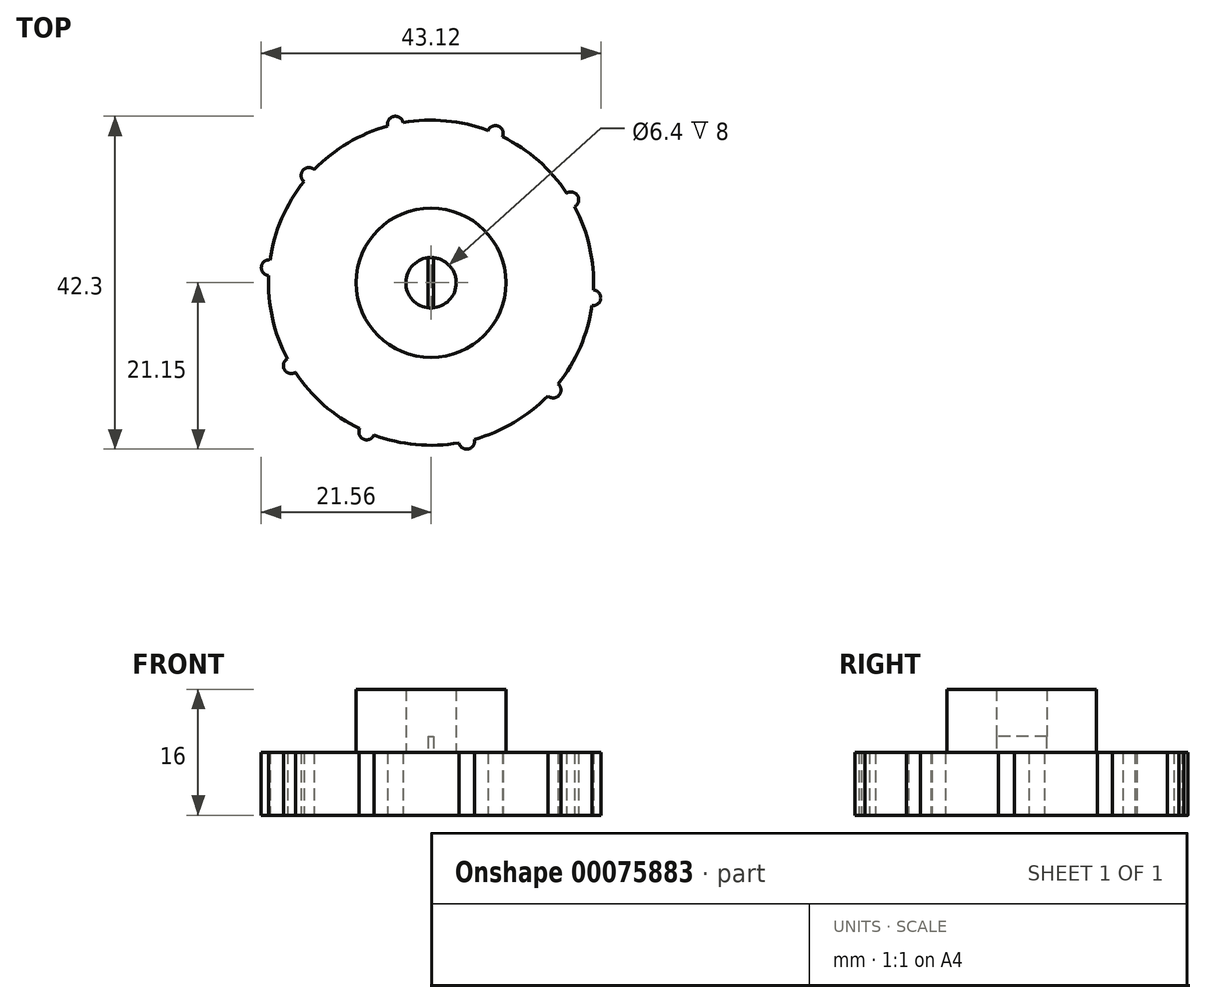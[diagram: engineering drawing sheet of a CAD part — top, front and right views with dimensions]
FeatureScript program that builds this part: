
annotation { "Feature Type Name" : "Feature", "Feature Type Description" : "" }
export const myFeature = defineFeature(function(context is Context, id is Id, definition is map)
    precondition{}
    {
        {
            var Q0;
            Q0=qCreatedBy(makeId("Top.planeOp"),FACE);
            var sketch = newSketch(context, id + "F0", { "sketchPlane" : qUnion([Q0])});
            skCircle(sketch, "E0", {"center": v(0, 0) * mm, "radius": 20.65 * mm});
            skCircle(sketch, "E1", {"center": v(-15.5, 13.63) * mm, "radius": 1 * mm});
            skCircle(sketch, "E2.1.0", {"center": v(-4.53, 20.15) * mm, "radius": 1 * mm});
            skCircle(sketch, "E2.2.0", {"center": v(8.17, 18.96) * mm, "radius": 1 * mm});
            skCircle(sketch, "E2.3.0", {"center": v(17.76, 10.54) * mm, "radius": 1 * mm});
            skCircle(sketch, "E2.4.0", {"center": v(20.56, -1.91) * mm, "radius": 1 * mm});
            skCircle(sketch, "E2.5.0", {"center": v(15.5, -13.63) * mm, "radius": 1 * mm});
            skCircle(sketch, "E2.6.0", {"center": v(4.53, -20.15) * mm, "radius": 1 * mm});
            skCircle(sketch, "E2.7.0", {"center": v(-8.17, -18.96) * mm, "radius": 1 * mm});
            skCircle(sketch, "E2.8.0", {"center": v(-17.76, -10.54) * mm, "radius": 1 * mm});
            skCircle(sketch, "E2.9.0", {"center": v(-20.56, 1.91) * mm, "radius": 1 * mm});
            skLineSegment(sketch, "E2.anchor1", {"start": v(0, 0) * mm, "end": v(-15.5, 13.63) * mm, "construction": true});
            skLineSegment(sketch, "E2.anchor2", {"start": v(0, 0) * mm, "end": v(-20.56, 1.91) * mm, "construction": true});
            skSolve(sketch);
        }
        {
            var Q0;
            Q0 = qSketchRegion(id + "F0", true);
            extrude(context, id + "F1", {"entities" : qUnion([Q0]), "depth" : 8 * mm});
        }
        {
            var Q0;
            Q0=makeQuery(id+"F1.opExtrude","CAP_FACE",FACE,{"disambiguationData":[OSD([sQuery(id+"F0.wireOp",EDGE,"E0")])],"isStart":false});
            var sketch = newSketch(context, id + "F2", { "sketchPlane" : qUnion([Q0])});
            skCircle(sketch, "E3", {"center": v(0, 0) * mm, "radius": 9.5 * mm});
            skCircle(sketch, "E4", {"center": v(0, 0) * mm, "radius": 3.2 * mm});
            skLineSegment(sketch, "E5.right", {"start": v(3.2, 0) * mm, "end": v(3.2, 0) * mm});
            skSolve(sketch);
        }
        {
            var Q0;
            Q0=makeQuery(id+"F2.imprint","IMPRINT",FACE,{"disambiguationData":[TD([[makeQuery(id+"F2.imprint","IMPRINT",EDGE,{"derivedFrom":sQuery(id+"F2.wireOp",EDGE,"E3")}),1.0]])]});
            extrude(context, id + "F3", {"entities" : qUnion([Q0]), "operationType" : NewBodyOperationType.ADD, "depth" : 8 * mm});
        }
        {
            var Q0;
            Q0=makeQuery(id+"F3.boolean.opBoolean","SPLIT",FACE,{"disambiguationData":[TD([makeQuery(id+"F3.opExtrude","SWEPT_FACE",FACE,{"disambiguationData":[OSD([sQuery(id+"F2.wireOp",EDGE,"E4")])]})])],"derivedFrom":makeQuery(id+"F1.opExtrude","CAP_FACE",FACE,{"disambiguationData":[OSD([sQuery(id+"F0.wireOp",EDGE,"E0")])],"isStart":false})});
            var sketch = newSketch(context, id + "F4", { "sketchPlane" : qUnion([Q0])});
            skLineSegment(sketch, "E6.bottom", {"start": v(-0.37, 3.22) * mm, "end": v(0.31, 3.22) * mm});
            skLineSegment(sketch, "E6.top", {"start": v(-0.37, -3.24) * mm, "end": v(0.31, -3.24) * mm});
            skLineSegment(sketch, "E6.left", {"start": v(-0.37, 3.22) * mm, "end": v(-0.37, -3.24) * mm});
            skLineSegment(sketch, "E6.right", {"start": v(0.31, 3.22) * mm, "end": v(0.31, -3.24) * mm});
            skSolve(sketch);
        }
        {
            var Q0;
            Q0 = qSketchRegion(id + "F4", true);
            extrude(context, id + "F5", {"entities" : qUnion([Q0]), "operationType" : NewBodyOperationType.ADD, "depth" : 2 * mm});
        }
    });
